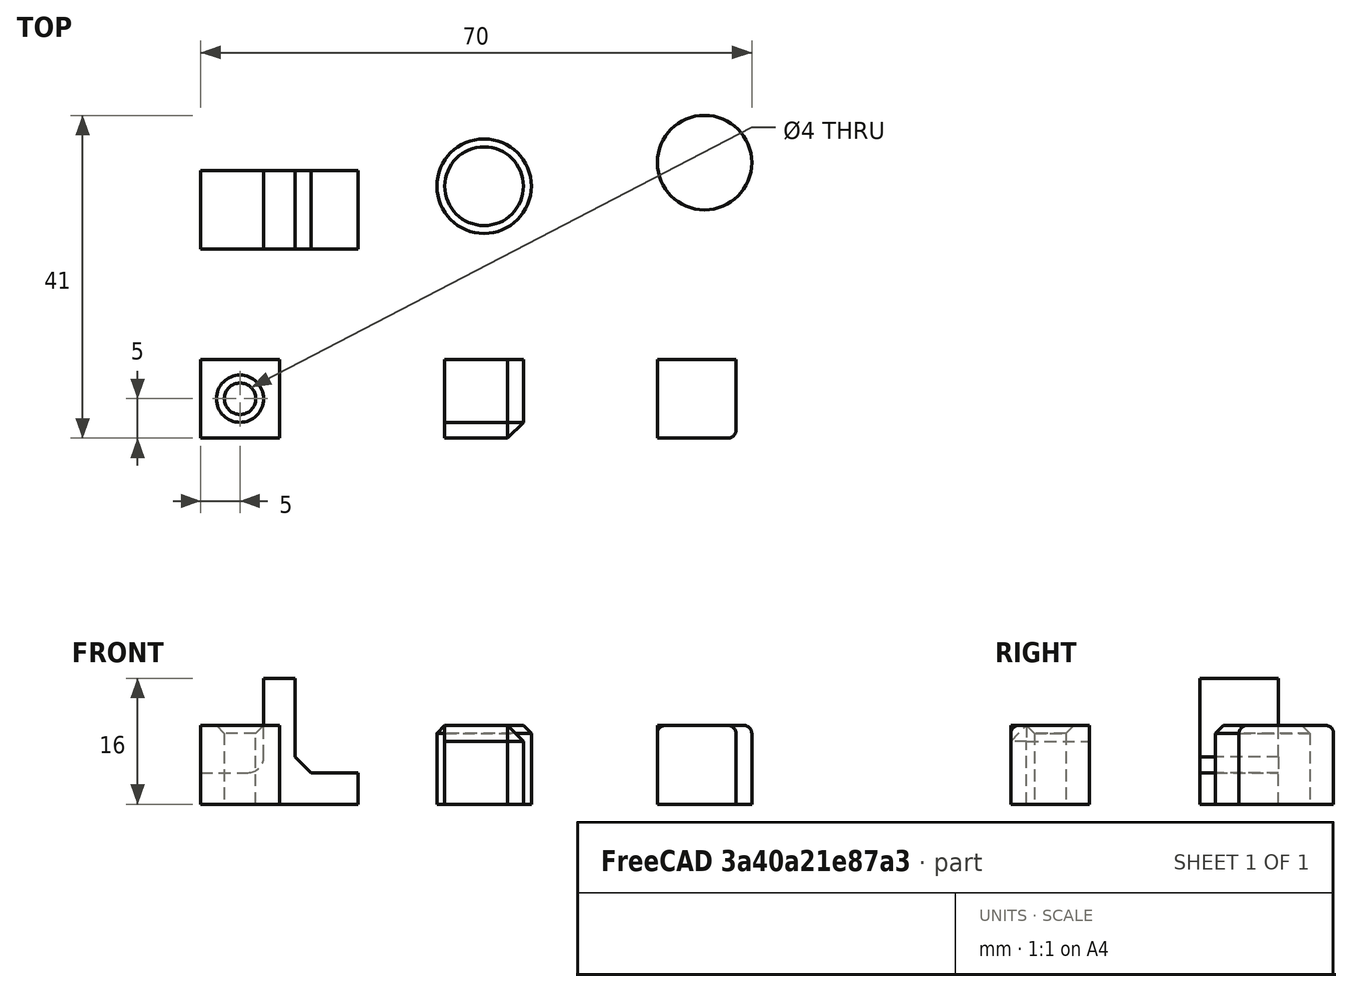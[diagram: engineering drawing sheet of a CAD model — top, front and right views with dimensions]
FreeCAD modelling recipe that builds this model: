
FCSTD DOCUMENT  (FreeCAD 1.0R39319 (Git))
Label: ojt1_t12p01_roundings_chamfers_reinforcements
License: All rights reserved
LicenseURL: https://en.wikipedia.org/wiki/All_rights_reserved
objects: Part::Box×5, Part::Chamfer×4, Part::Fillet×3, Part::Cylinder×3, Part::Cut×1, Part::MultiFuse×1
note: 17 computed .brp shape members not serialized (recipe doc carries the construction recipe); baked Part::Feature solids carry a one-line shape summary decoded from their .brp

FEATURE [Part::Box] Box  label="Cub"
  AttacherType = Attacher::AttachEngine3D
  Height = 10
  Length = 10
  Placement = pos=(40,0,0) rot=(0,0,1;0rad)
  Width = 10
FEATURE [Part::Fillet] Fillet
  Base = -> Box
  EdgeLinks = -> Box [Edge5,Edge6,Edge10]
  Edges = 3 edges r=1: [Edge5,Edge6,Edge10]
  Placement = pos=(18,0,0) rot=(0,0,1;0rad)
FEATURE [Part::Box] Box001  label="Cub001"
  AttacherType = Attacher::AttachEngine3D
  Height = 10
  Length = 10
  Placement = pos=(31,0,0) rot=(0,0,1;0rad)
  Width = 10
FEATURE [Part::Chamfer] Chamfer
  Base = -> Box001
  EdgeLinks = -> Box001 [Edge5,Edge6,Edge10]
  Edges = 3 edges r=2: [Edge5,Edge6,Edge10]
FEATURE [Part::Box] Box002  label="Cub002"
  AttacherType = Attacher::AttachEngine3D
  Height = 10
  Length = 10
  Width = 10
FEATURE [Part::Cylinder] Cylinder  label="Cilindre"
  Angle = 360
  AttacherType = Attacher::AttachEngine3D
  FirstAngle = 0
  Height = 10
  Placement = pos=(5,5,0) rot=(0,0,1;0rad)
  Radius = 2
  SecondAngle = 0
FEATURE [Part::Cut] Cut
  Base = -> Box002
  Tool = -> Cylinder
FEATURE [Part::Chamfer] Chamfer001
  Base = -> Cut
  EdgeLinks = -> Cut [Edge10]
  Edges = 1 edges r=1: [Edge10]
FEATURE [Part::Cylinder] Cylinder001  label="Cilindre001"
  Angle = 360
  AttacherType = Attacher::AttachEngine3D
  FirstAngle = 0
  Height = 10
  Placement = pos=(64,35,0) rot=(0,0,1;0rad)
  Radius = 6
  SecondAngle = 0
FEATURE [Part::Fillet] Fillet001
  Base = -> Cylinder001
  EdgeLinks = -> Cylinder001 [Edge3]
  Edges = 1 edges r=1: [Edge3]
FEATURE [Part::Cylinder] Cylinder002  label="Cilindre002"
  Angle = 360
  AttacherType = Attacher::AttachEngine3D
  FirstAngle = 0
  Height = 10
  Placement = pos=(36,32,0) rot=(0,0,1;0rad)
  Radius = 6
  SecondAngle = 0
FEATURE [Part::Chamfer] Chamfer002
  Base = -> Cylinder002
  EdgeLinks = -> Cylinder002 [Edge3]
  Edges = 1 edges r=1: [Edge3]
FEATURE [Part::Box] Box003  label="Cub003"
  AttacherType = Attacher::AttachEngine3D
  Height = 4
  Length = 20
  Placement = pos=(0,24,0) rot=(0,0,1;0rad)
  Width = 10
FEATURE [Part::Box] Box004  label="Cub004"
  AttacherType = Attacher::AttachEngine3D
  Height = 16
  Length = 4
  Placement = pos=(8,24,0) rot=(0,0,1;0rad)
  Width = 10
FEATURE [Part::MultiFuse] Fusion
  Refine = true
  Shapes = -> [Box004,Box003]
FEATURE [Part::Fillet] Fillet002
  Base = -> Fusion
  EdgeLinks = -> Fusion [Edge16]
  Edges = 1 edges r=2: [Edge16]
FEATURE [Part::Chamfer] Chamfer003
  Base = -> Fillet002
  EdgeLinks = -> Fillet002 [Edge24]
  Edges = 1 edges r=2: [Edge24]
